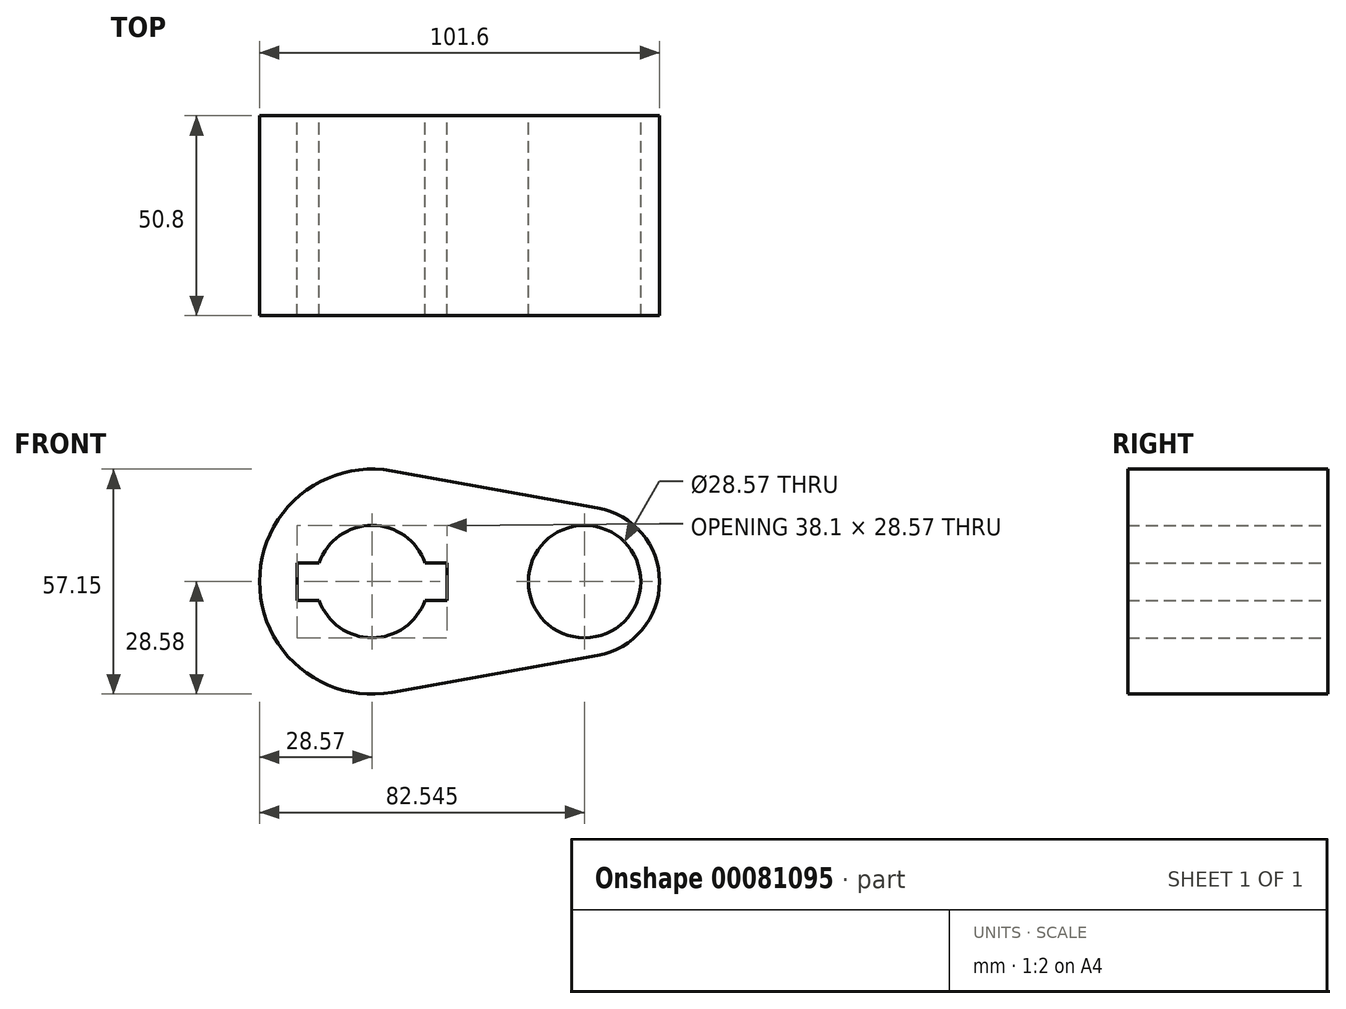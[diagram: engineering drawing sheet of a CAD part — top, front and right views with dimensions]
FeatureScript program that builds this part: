
annotation { "Feature Type Name" : "Feature", "Feature Type Description" : "" }
export const myFeature = defineFeature(function(context is Context, id is Id, definition is map)
    precondition{}
    {
        {
            var Q0;
            Q0=qCreatedBy(makeId("Front.planeOp"),FACE);
            var sketch = newSketch(context, id + "F0", { "sketchPlane" : qUnion([Q0])});
            skCircle(sketch, "E0", {"center": v(0, 0) * mm, "radius": 28.58 * mm});
            skCircle(sketch, "E1", {"center": v(53.97, 0) * mm, "radius": 19.05 * mm});
            skLineSegment(sketch, "E2", {"start": v(5.04, -28.13) * mm, "end": v(57.34, -18.75) * mm});
            skLineSegment(sketch, "E3", {"start": v(5.04, 28.13) * mm, "end": v(57.34, 18.75) * mm});
            skCircle(sketch, "E4", {"center": v(0, 0) * mm, "radius": 14.29 * mm});
            skCircle(sketch, "E5", {"center": v(53.97, 0) * mm, "radius": 14.29 * mm});
            skLineSegment(sketch, "E6.bottom", {"start": v(-19.05, 4.76) * mm, "end": v(19.05, 4.76) * mm});
            skLineSegment(sketch, "E6.top", {"start": v(-19.05, -4.76) * mm, "end": v(19.05, -4.76) * mm});
            skLineSegment(sketch, "E6.left", {"start": v(-19.05, 4.76) * mm, "end": v(-19.05, -4.76) * mm});
            skLineSegment(sketch, "E6.right", {"start": v(19.05, 4.76) * mm, "end": v(19.05, -4.76) * mm});
            skSolve(sketch);
        }
        {
            var Q0;
            {var subQ11=sQuery(id+"F0.wireOp",EDGE,"E6.left");Q0=makeQuery(id+"F0.imprint","IMPRINT",FACE,{"disambiguationData":[TD([[makeQuery(id+"F0.imprint","IMPRINT",EDGE,{"derivedFrom":subQ11}),-1.0]])]});}
            var Q1;
            Q1=makeQuery(id+"F0.imprint","IMPRINT",FACE,{"disambiguationData":[TD([[makeQuery(id+"F0.imprint","IMPRINT",EDGE,{"derivedFrom":sQuery(id+"F0.wireOp",EDGE,"E5")}),-1.0]])]});
            var Q2;
            {var subQ0=sQuery(id+"F0.wireOp",EDGE,"E2");Q2=makeQuery(id+"F0.imprint","IMPRINT",FACE,{"disambiguationData":[TD([[makeQuery(id+"F0.imprint","IMPRINT",EDGE,{"derivedFrom":subQ0}),1.0]])]});}
            extrude(context, id + "F1", {"entities" : qUnion([Q0, Q1, Q2]), "depth" : 25.4 * mm});
        }
        {
            var Q0;
            Q0 = qSketchRegion(id + "F0", true);
            extrude(context, id + "F2", {"entities" : qUnion([Q0]), "operationType" : NewBodyOperationType.ADD, "depth" : 50.8 * mm});
        }
    });
